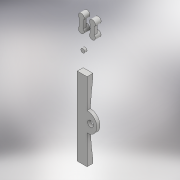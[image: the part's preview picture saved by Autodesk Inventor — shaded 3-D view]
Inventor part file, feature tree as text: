
AUTODESK INVENTOR PART (.ipt)
format: ipt  version: 2017 (Build 210142000, 142)  size: 170,496 bytes
history: native  units: mm
features: extrude x6, sketch x6
ambient origin geometry x8: Origin, YZ Plane, XZ Plane, XY Plane, X Axis, Y Axis, Z Axis, Center Point
bodies: Solid1 (feature_tree)
feature tree (12):
  extrude  "Extrusion1"  Depth=5.0mm
  extrude  "Extrusion2"  Depth=3.0mm
  extrude  "Extrusion3"  Depth=10.0mm TaperAngle=0.0deg
  extrude  "Extrusion4"  Depth=10.0mm TaperAngle=0.0deg
  extrude  "Extrusion6"  Depth=3.0mm
  extrude  "Extrusion7"  Depth=3.0mm
  sketch  "Sketch1"  dims[d0=5.0mm d1=40.0mm]
  sketch  "Sketch2"  dims[d2=3.0mm d3=0.0mm d4=2.0mm]
  sketch  "Sketch3"  dims[d5=2.0mm d6=10.0mm d7=0.0mm]
  sketch  "Sketch4"  dims[d8=3.0mm d9=10.0mm d10=0.0mm]
  sketch  "Sketch6"  dims[d11=3.0mm d14=3.0mm]
  sketch  "Sketch7"  dims[d17=3.0mm d18=3.0mm d19=1.5mm d20=0.0mm d27=2.0mm d28=1.2mm d29=0.0mm d30=3.0mm d31=3.0mm d32=3.0mm d33=3.0mm d34=3.0mm d35=0.0mm]
